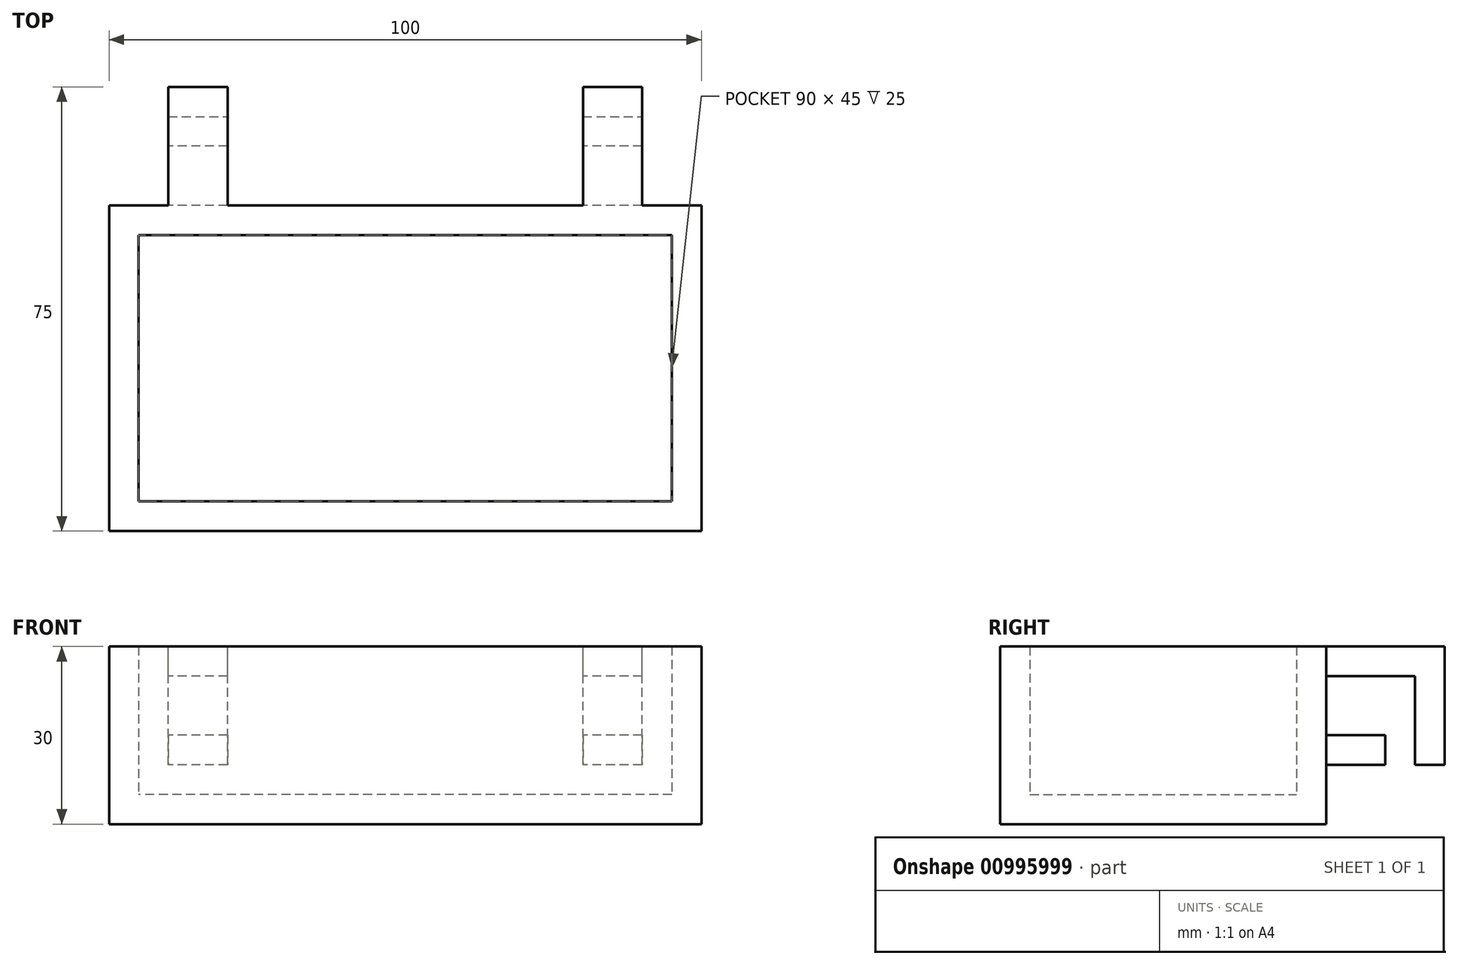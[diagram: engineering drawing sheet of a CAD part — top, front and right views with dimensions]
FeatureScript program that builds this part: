
annotation { "Feature Type Name" : "Feature", "Feature Type Description" : "" }
export const myFeature = defineFeature(function(context is Context, id is Id, definition is map)
    precondition{}
    {
        {
            var Q0;
            Q0=qCreatedBy(makeId("Top.planeOp"),FACE);
            var sketch = newSketch(context, id + "F0", { "sketchPlane" : qUnion([Q0])});
            skLineSegment(sketch, "E0.bottom", {"start": v(0, 0) * mm, "end": v(-90, 0) * mm});
            skLineSegment(sketch, "E0.top", {"start": v(0, 45) * mm, "end": v(-90, 45) * mm});
            skLineSegment(sketch, "E0.left", {"start": v(0, 0) * mm, "end": v(0, 45) * mm});
            skLineSegment(sketch, "E0.right", {"start": v(-90, 0) * mm, "end": v(-90, 45) * mm});
            skLineSegment(sketch, "E1.0", {"start": v(5, 50) * mm, "end": v(-95, 50) * mm});
            skLineSegment(sketch, "E1.1", {"start": v(5, -5) * mm, "end": v(5, 50) * mm});
            skLineSegment(sketch, "E1.2", {"start": v(5, -5) * mm, "end": v(-95, -5) * mm});
            skLineSegment(sketch, "E1.3", {"start": v(-95, -5) * mm, "end": v(-95, 50) * mm});
            skSolve(sketch);
        }
        {
            var Q0;
            Q0=makeQuery(id+"F0.imprint","IMPRINT",FACE,{"disambiguationData":[TD([[makeQuery(id+"F0.imprint","IMPRINT",EDGE,{"derivedFrom":sQuery(id+"F0.wireOp",EDGE,"E0.bottom")}),-1.0]])]});
            extrude(context, id + "F1", {"entities" : qUnion([Q0]), "depth" : 5 * mm, "offsetDistance" : 25 * mm});
        }
        {
            var Q0;
            Q0=makeQuery(id+"F0.imprint","IMPRINT",FACE,{"disambiguationData":[TD([[makeQuery(id+"F0.imprint","IMPRINT",EDGE,{"derivedFrom":sQuery(id+"F0.wireOp",EDGE,"E0.bottom")}),1.0]])]});
            extrude(context, id + "F2", {"entities" : qUnion([Q0]), "operationType" : NewBodyOperationType.ADD, "depth" : 30 * mm, "offsetDistance" : 25 * mm});
        }
        {
            var Q0;
            Q0=makeQuery(id+"F2.opExtrude","CAP_FACE",FACE,{"disambiguationData":[OSD([sQuery(id+"F0.wireOp",EDGE,"E0.bottom"),sQuery(id+"F0.wireOp",EDGE,"E0.top"),sQuery(id+"F0.wireOp",EDGE,"E0.left"),sQuery(id+"F0.wireOp",EDGE,"E0.right"),sQuery(id+"F0.wireOp",EDGE,"E1.0"),sQuery(id+"F0.wireOp",EDGE,"E1.1"),sQuery(id+"F0.wireOp",EDGE,"E1.2"),sQuery(id+"F0.wireOp",EDGE,"E1.3"),sQuery(id+"F0.wireOp",EDGE,"ztCPllvv-muVx-NdKB-kmjH-apVXouv4jIEj.bottom"),sQuery(id+"F0.wireOp",EDGE,"GInIVkHl-crYS-fz5E-cHp8-sXC6BDvZoK3y.bottom")])],"isStart":false});
            var sketch = newSketch(context, id + "F3", { "sketchPlane" : qUnion([Q0])});
            skLineSegment(sketch, "E2.bottom", {"start": v(-85, 70) * mm, "end": v(-75, 70) * mm});
            skLineSegment(sketch, "E2.top", {"start": v(-85, 50) * mm, "end": v(-75, 50) * mm});
            skLineSegment(sketch, "E2.left", {"start": v(-85, 70) * mm, "end": v(-85, 50) * mm});
            skLineSegment(sketch, "E2.right", {"start": v(-75, 70) * mm, "end": v(-75, 50) * mm});
            skLineSegment(sketch, "E3.bottom", {"start": v(-15, 70) * mm, "end": v(-5, 70) * mm});
            skLineSegment(sketch, "E3.top", {"start": v(-15, 50) * mm, "end": v(-5, 50) * mm});
            skLineSegment(sketch, "E3.left", {"start": v(-15, 70) * mm, "end": v(-15, 50) * mm});
            skLineSegment(sketch, "E3.right", {"start": v(-5, 70) * mm, "end": v(-5, 50) * mm});
            skLineSegment(sketch, "E4", {"start": v(-85, 65) * mm, "end": v(-75, 65) * mm});
            skLineSegment(sketch, "E5", {"start": v(-15, 65) * mm, "end": v(-5, 65) * mm});
            skSolve(sketch);
        }
        {
            var Q0;
            {var subQ0=sQuery(id+"F3.wireOp",EDGE,"E2.top");Q0=makeQuery(id+"F3.imprint","IMPRINT",FACE,{"disambiguationData":[TD([[makeQuery(id+"F3.imprint","IMPRINT",EDGE,{"derivedFrom":subQ0}),-1.0]])]});}
            var Q1;
            {var subQ0=sQuery(id+"F3.wireOp",EDGE,"E2.bottom");Q1=makeQuery(id+"F3.imprint","IMPRINT",FACE,{"disambiguationData":[TD([[makeQuery(id+"F3.imprint","IMPRINT",EDGE,{"derivedFrom":subQ0}),-1.0]])]});}
            var Q2;
            {var subQ0=sQuery(id+"F3.wireOp",EDGE,"E3.top");Q2=makeQuery(id+"F3.imprint","IMPRINT",FACE,{"disambiguationData":[TD([[makeQuery(id+"F3.imprint","IMPRINT",EDGE,{"derivedFrom":subQ0}),-1.0]])]});}
            var Q3;
            {var subQ0=sQuery(id+"F3.wireOp",EDGE,"E3.bottom");Q3=makeQuery(id+"F3.imprint","IMPRINT",FACE,{"disambiguationData":[TD([[makeQuery(id+"F3.imprint","IMPRINT",EDGE,{"derivedFrom":subQ0}),-1.0]])]});}
            extrude(context, id + "F4", {"entities" : qUnion([Q0, Q1, Q2, Q3]), "operationType" : NewBodyOperationType.ADD, "oppositeDirection" : true, "depth" : 5 * mm, "offsetDistance" : 25 * mm});
        }
        {
            var Q0;
            {var subQ0=sQuery(id+"F3.wireOp",EDGE,"E2.bottom");Q0=makeQuery(id+"F3.imprint","IMPRINT",FACE,{"disambiguationData":[TD([[makeQuery(id+"F3.imprint","IMPRINT",EDGE,{"derivedFrom":subQ0}),-1.0]])]});}
            var Q1;
            {var subQ0=sQuery(id+"F3.wireOp",EDGE,"E3.bottom");Q1=makeQuery(id+"F3.imprint","IMPRINT",FACE,{"disambiguationData":[TD([[makeQuery(id+"F3.imprint","IMPRINT",EDGE,{"derivedFrom":subQ0}),-1.0]])]});}
            extrude(context, id + "F5", {"entities" : qUnion([Q0, Q1]), "operationType" : NewBodyOperationType.ADD, "oppositeDirection" : true, "depth" : 20 * mm, "offsetDistance" : 25 * mm});
        }
        {
            var Q0;
            Q0=makeQuery(id+"F2.opExtrude","SWEPT_FACE",FACE,{"disambiguationData":[OSD([sQuery(id+"F0.wireOp",EDGE,"E1.0")])]});
            var sketch = newSketch(context, id + "F6", { "sketchPlane" : qUnion([Q0])});
            skLineSegment(sketch, "E6.bottom", {"start": v(5, 15) * mm, "end": v(15, 15) * mm});
            skLineSegment(sketch, "E6.top", {"start": v(5, 10) * mm, "end": v(15, 10) * mm});
            skLineSegment(sketch, "E6.left", {"start": v(5, 15) * mm, "end": v(5, 10) * mm});
            skLineSegment(sketch, "E6.right", {"start": v(15, 15) * mm, "end": v(15, 10) * mm});
            skLineSegment(sketch, "E7.bottom", {"start": v(75, 15) * mm, "end": v(85, 15) * mm});
            skLineSegment(sketch, "E7.top", {"start": v(75, 10) * mm, "end": v(85, 10) * mm});
            skLineSegment(sketch, "E7.left", {"start": v(75, 15) * mm, "end": v(75, 10) * mm});
            skLineSegment(sketch, "E7.right", {"start": v(85, 15) * mm, "end": v(85, 10) * mm});
            skSolve(sketch);
        }
        {
            var Q0;
            Q0=makeQuery(id+"F6.imprint","IMPRINT",FACE,{"disambiguationData":[TD([[makeQuery(id+"F6.imprint","IMPRINT",EDGE,{"derivedFrom":sQuery(id+"F6.wireOp",EDGE,"E6.bottom")}),-1.0]])]});
            var Q1;
            Q1=makeQuery(id+"F6.imprint","IMPRINT",FACE,{"disambiguationData":[TD([[makeQuery(id+"F6.imprint","IMPRINT",EDGE,{"derivedFrom":sQuery(id+"F6.wireOp",EDGE,"E7.bottom")}),-1.0]])]});
            extrude(context, id + "F7", {"entities" : qUnion([Q0, Q1]), "operationType" : NewBodyOperationType.ADD, "depth" : 10 * mm, "offsetDistance" : 25 * mm});
        }
    });
